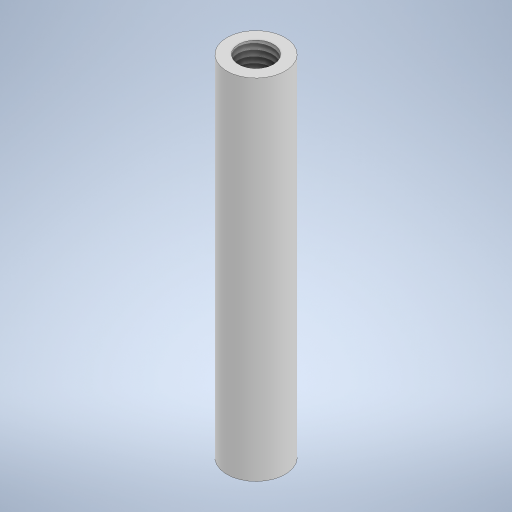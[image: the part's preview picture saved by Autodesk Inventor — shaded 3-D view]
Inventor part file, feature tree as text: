
AUTODESK INVENTOR PART (.ipt)
format: ipt  version: 2023 (Build 270158000, 158)  size: 228,864 bytes
history: native  units: mm
features: other x1, extrude x1, thread x1, sketch x1
ambient origin geometry x8: Origin, YZ Plane, XZ Plane, XY Plane, X Axis, Y Axis, Z Axis, Center Point
bodies: Body1 (feature_tree)
feature tree (4):
  other  "Твердое тело1"
  extrude  "Выдавливание1"  Depth=3.0mm
  thread  "Резьба1"
  sketch  "Эскиз1"
